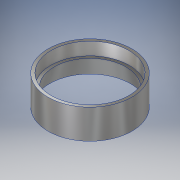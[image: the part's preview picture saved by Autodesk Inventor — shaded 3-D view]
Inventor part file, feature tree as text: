
AUTODESK INVENTOR PART (.ipt)
format: ipt  version: 2017 (Build 210142000, 142)  size: 138,752 bytes
history: native  units: in
note: dims shown in document units (in); Inventor stores cm internally (conversion verified against a paired STEP export)
features: revolve x1, sketch x1
ambient origin geometry x8: Origin, YZ Plane, XZ Plane, XY Plane, X Axis, Y Axis, Z Axis, Center Point
bodies: Solid1 (feature_tree)
feature tree (2):
  revolve  "Revolution1"  [1 undecoded]
  sketch  "Sketch1"  dims[d0=0.25in d1=0.125in d2=105.0deg d3=3.0in d4=0.25in d5=90.0deg d6=2.46in]
note: 1 required parameter value undecoded (feature->parameter linkage not recoverable at this tier; creation-order binding heuristic only, values carry confidence <= 0.55)
